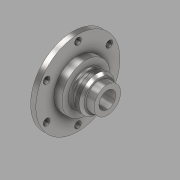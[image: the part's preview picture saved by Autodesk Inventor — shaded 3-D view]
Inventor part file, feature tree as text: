
AUTODESK INVENTOR PART (.ipt)
format: ipt  version: 2020 (Build 240168000, 168)  size: 178,688 bytes
history: native  units: mm
features: sketch x3, hole x2, other x1, revolve x1, thread x1, fillet x1
ambient origin geometry x8: Origin, YZ Plane, XZ Plane, XY Plane, X Axis, Y Axis, Z Axis, Center Point
bodies: Body1 (feature_tree)
feature tree (9):
  other  "Sólido1"
  revolve  "Revolución1"  [1 undecoded]
  hole  "Agujero1"  [1 undecoded]
  hole  "Agujero2"  [1 undecoded]
  thread  "Rosca1"  [1 undecoded]
  fillet  "Empalme1"  Radius=21.0mm
  sketch  "Boceto1"  dims[d0=50.0mm d1=6.2mm]
  sketch  "Boceto2"  dims[d2=9.6mm d3=28.5mm]
  sketch  "Boceto3"  dims[d4=6.5mm d5=3.0mm d8=18.0mm d10=21.0mm d11=60.0deg d12=18.0mm d14=9.4mm d15=135.0deg d16=9.5mm d17=41.2mm d18=15.8mm d19=90.0deg d20=20.0mm d21=6.35mm d22=44.5mm d23=9.5mm d24=90.0deg d25=8.0mm d26=20.594885mm d27=43.0mm d28=7.9mm d29=6.35mm d30=44.5mm d31=9.5mm d32=90.0deg d33=8.0mm d34=20.594885mm d35=60.0mm d37=360.0deg d39=4.668mm d40=0.0mm d41=2.0mm]
note: 4 required parameter values undecoded (feature->parameter linkage not recoverable at this tier; creation-order binding heuristic only, values carry confidence <= 0.55)